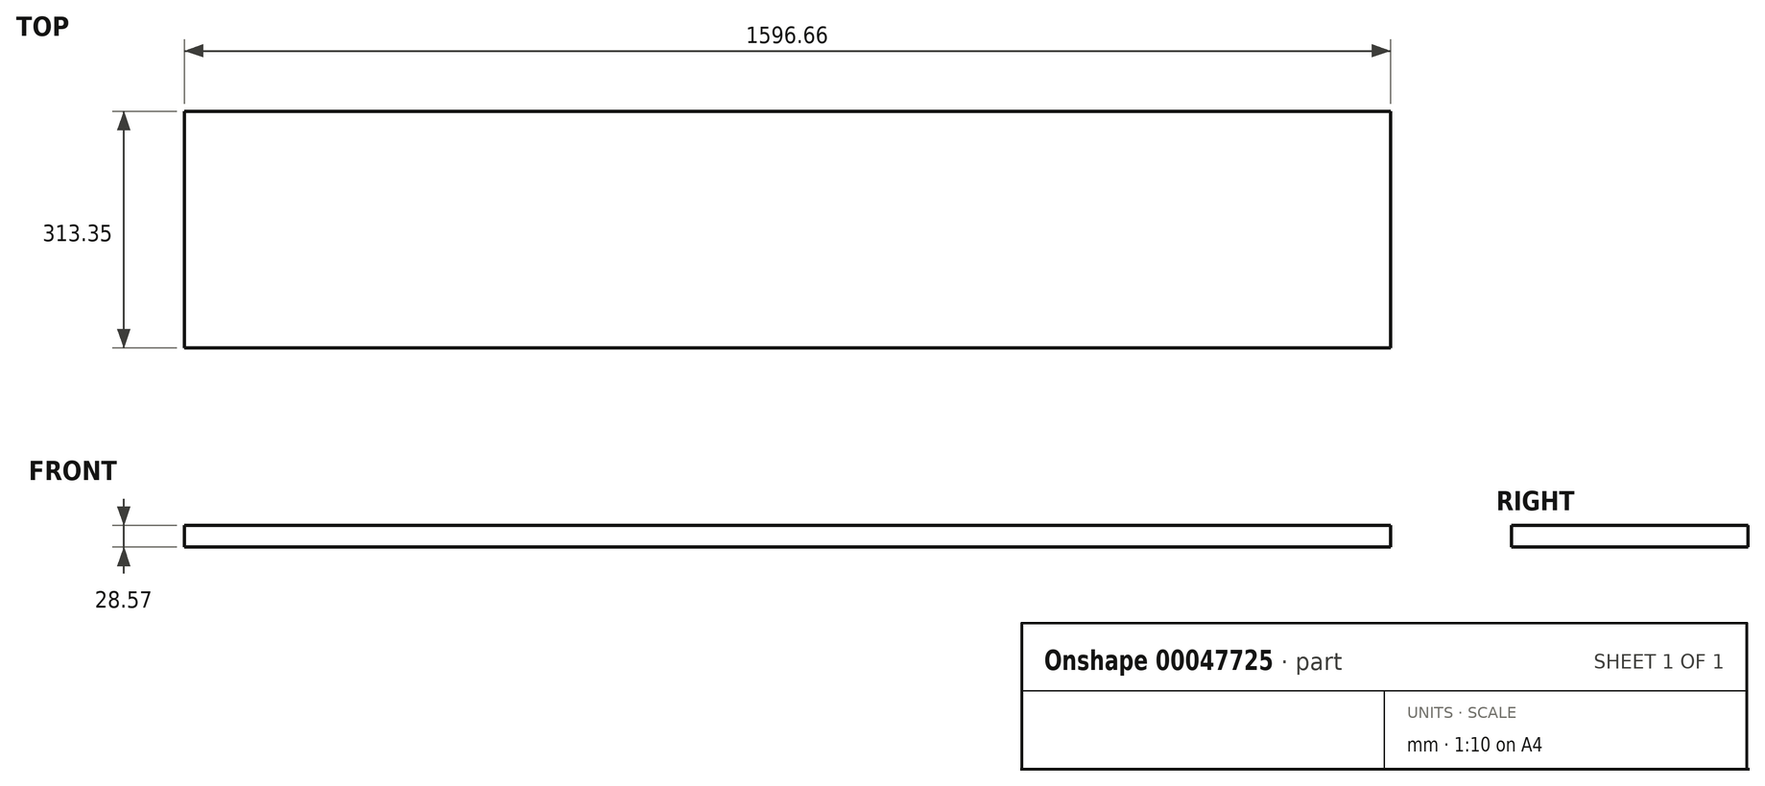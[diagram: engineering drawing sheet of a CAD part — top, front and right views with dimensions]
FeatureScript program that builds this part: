
annotation { "Feature Type Name" : "Feature", "Feature Type Description" : "" }
export const myFeature = defineFeature(function(context is Context, id is Id, definition is map)
    precondition{}
    {
        {
            var Q0;
            Q0=qCreatedBy(makeId("Top.planeOp"),FACE);
            var sketch = newSketch(context, id + "F0", { "sketchPlane" : qUnion([Q0])});
            skLineSegment(sketch, "E0.bottom", {"start": v(-746.92, 185.84) * mm, "end": v(849.74, 185.84) * mm});
            skLineSegment(sketch, "E0.top", {"start": v(-746.92, -127.51) * mm, "end": v(849.74, -127.51) * mm});
            skLineSegment(sketch, "E0.left", {"start": v(-746.92, 185.84) * mm, "end": v(-746.92, -127.51) * mm});
            skLineSegment(sketch, "E0.right", {"start": v(849.74, 185.84) * mm, "end": v(849.74, -127.51) * mm});
            skSolve(sketch);
        }
        {
            var Q0;
            Q0=makeQuery(id+"F0.imprint","IMPRINT",FACE,{"disambiguationData":[TD([[makeQuery(id+"F0.imprint","IMPRINT",EDGE,{"derivedFrom":sQuery(id+"F0.wireOp",EDGE,"E0.bottom")}),-1.0]])]});
            extrude(context, id + "F1", {"entities" : qUnion([Q0]), "depth" : 28.57 * mm});
        }
    });
